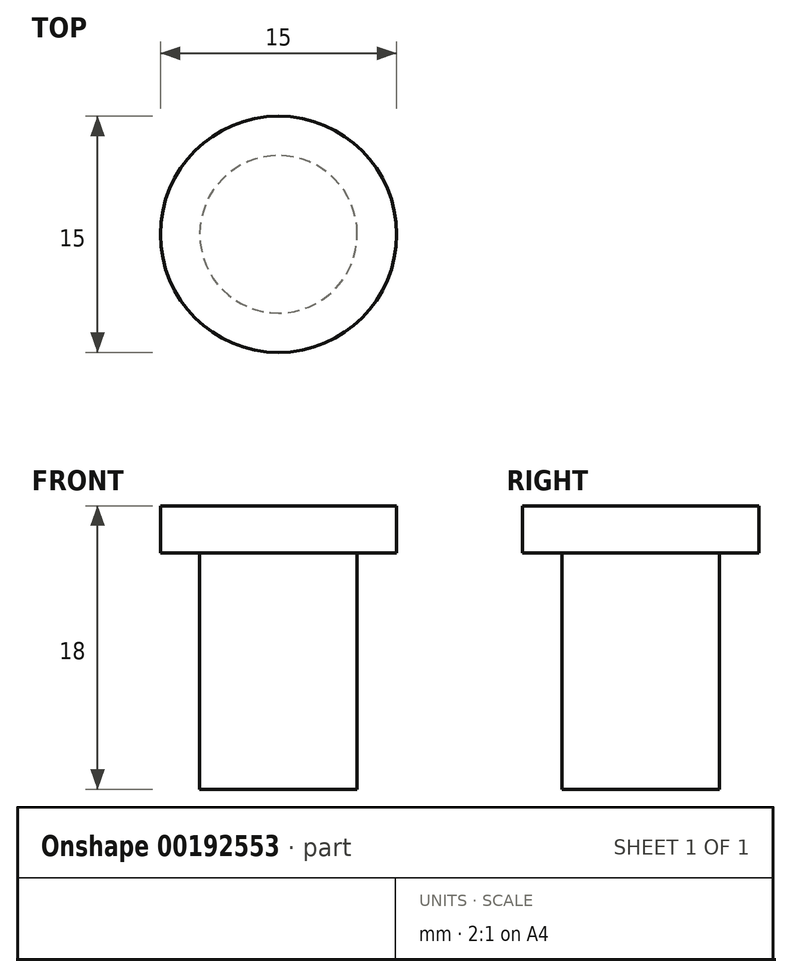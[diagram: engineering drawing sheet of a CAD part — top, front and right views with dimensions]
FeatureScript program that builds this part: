
annotation { "Feature Type Name" : "Feature", "Feature Type Description" : "" }
export const myFeature = defineFeature(function(context is Context, id is Id, definition is map)
    precondition{}
    {
        {
            var Q0;
            Q0=qCreatedBy(makeId("Top.planeOp"),FACE);
            var sketch = newSketch(context, id + "F0", { "sketchPlane" : qUnion([Q0])});
            skCircle(sketch, "E0", {"center": v(0, 0) * mm, "radius": 5 * mm});
            skSolve(sketch);
        }
        {
            var Q0;
            Q0 = qSketchRegion(id + "F0", true);
            extrude(context, id + "F1", {"entities" : qUnion([Q0]), "depth" : 18 * mm});
        }
        {
            var Q0;
            Q0=makeQuery(id+"F1.opExtrude","CAP_FACE",FACE,{"disambiguationData":[OSD([sQuery(id+"F0.wireOp",EDGE,"E0")])],"isStart":false});
            var sketch = newSketch(context, id + "F2", { "sketchPlane" : qUnion([Q0])});
            skCircle(sketch, "E1", {"center": v(0, 0) * mm, "radius": 7.5 * mm});
            skSolve(sketch);
        }
        {
            var Q0;
            Q0 = qSketchRegion(id + "F2", true);
            extrude(context, id + "F3", {"entities" : qUnion([Q0]), "operationType" : NewBodyOperationType.ADD, "oppositeDirection" : true, "depth" : 3 * mm});
        }
    });
